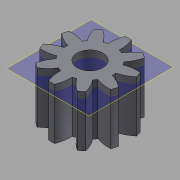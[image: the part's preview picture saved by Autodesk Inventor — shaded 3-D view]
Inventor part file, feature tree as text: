
AUTODESK INVENTOR PART (.ipt)
format: ipt  version: 2015 (Build 190159000, 159)  size: 168,448 bytes
history: native  units: in
note: dims shown in document units (in); Inventor stores cm internally (conversion verified against a paired STEP export)
features: other x13, sketch x3, plane x2
ambient origin geometry x8: Origin, YZ Plane, XZ Plane, XY Plane, X Axis, Y Axis, Z Axis, Center Point
bodies: Solid1 (feature_tree)
feature tree (18):
  other  "Spur Gear18_MIR4.ipt"
  other  "Solid1::Spur Gear18_MIR4.ipt"
  other  "TaggingFeature1"
  sketch  "Sketch1"  dims[d0=0.3937in]
  sketch  "Sketch2"  dims[d16=0.4528in d17=0.0in d41=0.0in d43=0.4528in d46=0.4528in d47=0.0in d48=0.0in]
  sketch  "Sketch3"
  plane  "XZ Plane_1"
  plane  "Work Plane2"
  other  "Z Axis_1"
  other  "Srf1"
  other  "Srf1::Derived"
  other  "Distance iMate"
  other  "Align iMate"
  other  "Mesh iMate"
  other  "Axis iMate"
  other  "Position iMate"
  other  "Mesh iMate2"
  other  "Start plane iMate"
